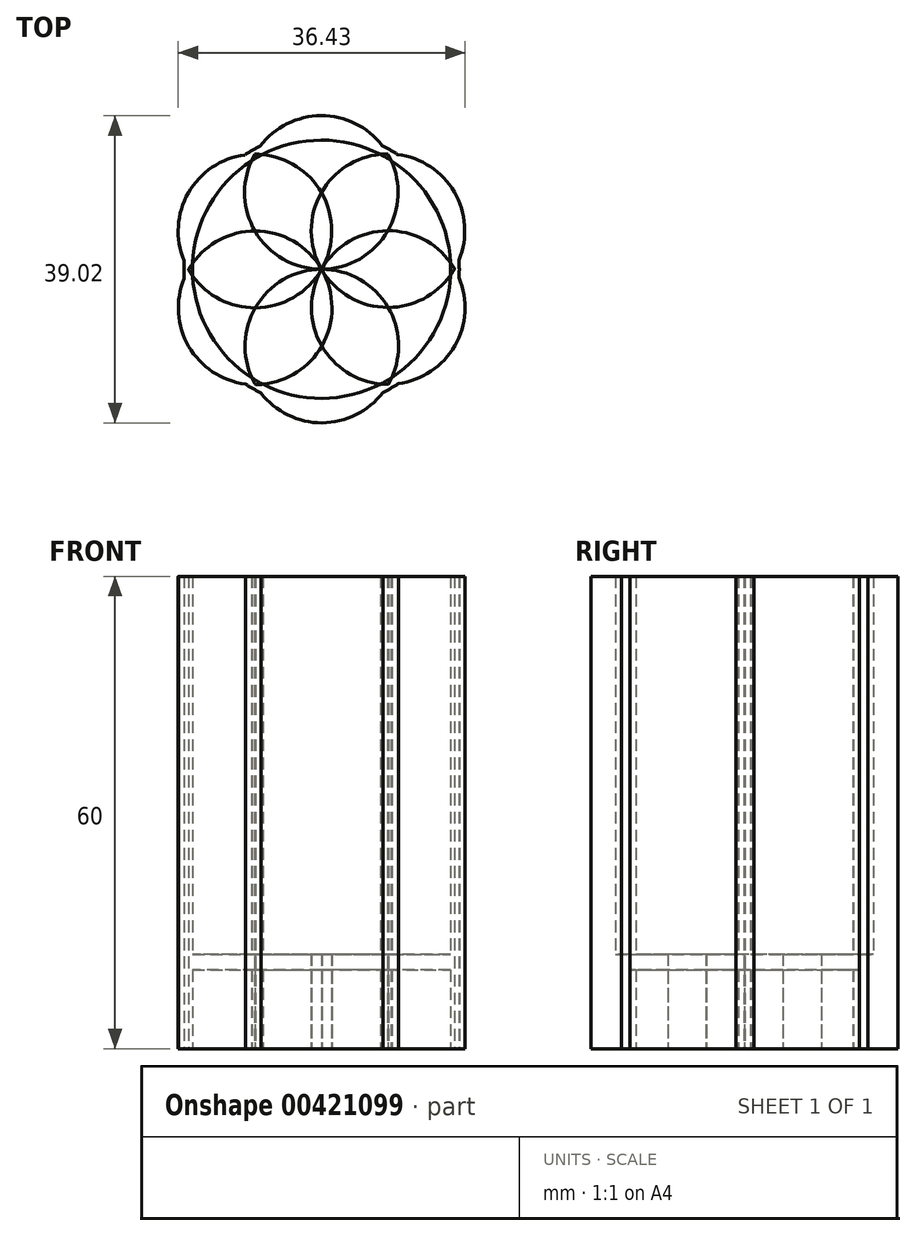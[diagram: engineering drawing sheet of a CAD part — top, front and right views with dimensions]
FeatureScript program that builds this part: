
annotation { "Feature Type Name" : "Feature", "Feature Type Description" : "" }
export const myFeature = defineFeature(function(context is Context, id is Id, definition is map)
    precondition{}
    {
        {
            var Q0;
            Q0=qCreatedBy(makeId("Top.planeOp"),FACE);
            var sketch = newSketch(context, id + "F0", { "sketchPlane" : qUnion([Q0])});
            skCircle(sketch, "E0", {"center": v(-40.7, 11.8) * mm, "radius": 9.75 * mm});
            skCircle(sketch, "E1", {"center": v(-32.26, 16.7) * mm, "radius": 9.75 * mm});
            skCircle(sketch, "E2", {"center": v(-32.23, 6.95) * mm, "radius": 9.75 * mm});
            skCircle(sketch, "E3", {"center": v(-40.66, 2.05) * mm, "radius": 9.75 * mm});
            skCircle(sketch, "E4", {"center": v(-49.13, 6.9) * mm, "radius": 9.75 * mm});
            skCircle(sketch, "E5", {"center": v(-49.15, 16.66) * mm, "radius": 9.75 * mm});
            skCircle(sketch, "E6", {"center": v(-40.72, 21.56) * mm, "radius": 9.75 * mm});
            skCircle(sketch, "E7", {"center": v(-40.7, 11.8) * mm, "radius": 13.06 * mm});
            skCircle(sketch, "E8", {"center": v(-40.7, 11.8) * mm, "radius": 14.2 * mm});
            skCircle(sketch, "E9", {"center": v(-40.7, 11.8) * mm, "radius": 15.33 * mm});
            skCircle(sketch, "E10", {"center": v(-40.7, 11.8) * mm, "radius": 16.4 * mm});
            skCircle(sketch, "E11", {"center": v(-40.7, 11.8) * mm, "radius": 17.5 * mm});
            skSolve(sketch);
        }
        {
            var Q0;
            Q0 = qSketchRegion(id + "F0", true);
            extrude(context, id + "F1", {"entities" : qUnion([Q0]), "depth" : 60 * mm});
        }
        {
            var Q0;
            {var subQ0=sQuery(id+"F0.wireOp",EDGE,"E9");var subQ1=sQuery(id+"F0.wireOp",EDGE,"E1");var subQ2=makeQuery(id+"F0.imprint","INTERSECT",VERTEX,{"disambiguationData":[OD(1.0)],"derivedFrom":[subQ1,subQ0]});Q0=makeQuery(id+"F0.imprint","IMPRINT",FACE,{"disambiguationData":[TD([[makeQuery(id+"F0.imprint","IMPRINT",EDGE,{"disambiguationData":[TD([[subQ2,-1.0]])],"derivedFrom":subQ1}),-1.0]])]});}
            var Q1;
            {var subQ0=sQuery(id+"F0.wireOp",EDGE,"E9");var subQ1=sQuery(id+"F0.wireOp",EDGE,"E2");var subQ2=makeQuery(id+"F0.imprint","INTERSECT",VERTEX,{"disambiguationData":[OD(1.0)],"derivedFrom":[subQ1,subQ0]});Q1=makeQuery(id+"F0.imprint","IMPRINT",FACE,{"disambiguationData":[TD([[makeQuery(id+"F0.imprint","IMPRINT",EDGE,{"disambiguationData":[TD([[subQ2,-1.0]])],"derivedFrom":subQ1}),-1.0]])]});}
            var Q2;
            {var subQ0=sQuery(id+"F0.wireOp",EDGE,"E10");var subQ1=sQuery(id+"F0.wireOp",EDGE,"E2");var subQ2=makeQuery(id+"F0.imprint","INTERSECT",VERTEX,{"disambiguationData":[OD(0.0)],"derivedFrom":[subQ1,subQ0]});Q2=makeQuery(id+"F0.imprint","IMPRINT",FACE,{"disambiguationData":[TD([[makeQuery(id+"F0.imprint","IMPRINT",EDGE,{"disambiguationData":[TD([[subQ2,-1.0]])],"derivedFrom":subQ1}),-1.0]])]});}
            var Q3;
            {var subQ0=sQuery(id+"F0.wireOp",EDGE,"E9");var subQ1=sQuery(id+"F0.wireOp",EDGE,"E2");var subQ2=makeQuery(id+"F0.imprint","INTERSECT",VERTEX,{"disambiguationData":[OD(0.0)],"derivedFrom":[subQ1,subQ0]});Q3=makeQuery(id+"F0.imprint","IMPRINT",FACE,{"disambiguationData":[TD([[makeQuery(id+"F0.imprint","IMPRINT",EDGE,{"disambiguationData":[TD([[subQ2,-1.0]])],"derivedFrom":subQ1}),-1.0]])]});}
            var Q4;
            {var subQ0=sQuery(id+"F0.wireOp",EDGE,"E8");var subQ1=sQuery(id+"F0.wireOp",EDGE,"E1");var subQ2=makeQuery(id+"F0.imprint","INTERSECT",VERTEX,{"disambiguationData":[OD(1.0)],"derivedFrom":[subQ1,subQ0]});Q4=makeQuery(id+"F0.imprint","IMPRINT",FACE,{"disambiguationData":[TD([[makeQuery(id+"F0.imprint","IMPRINT",EDGE,{"disambiguationData":[TD([[subQ2,-1.0]])],"derivedFrom":subQ1}),-1.0]])]});}
            var Q5;
            {var subQ0=sQuery(id+"F0.wireOp",EDGE,"E8");var subQ1=sQuery(id+"F0.wireOp",EDGE,"E2");var subQ2=makeQuery(id+"F0.imprint","INTERSECT",VERTEX,{"disambiguationData":[OD(1.0)],"derivedFrom":[subQ1,subQ0]});Q5=makeQuery(id+"F0.imprint","IMPRINT",FACE,{"disambiguationData":[TD([[makeQuery(id+"F0.imprint","IMPRINT",EDGE,{"disambiguationData":[TD([[subQ2,-1.0]])],"derivedFrom":subQ1}),-1.0]])]});}
            var Q6;
            {var subQ0=sQuery(id+"F0.wireOp",EDGE,"E7");var subQ1=sQuery(id+"F0.wireOp",EDGE,"E2");var subQ2=makeQuery(id+"F0.imprint","INTERSECT",VERTEX,{"disambiguationData":[OD(1.0)],"derivedFrom":[subQ1,subQ0]});Q6=makeQuery(id+"F0.imprint","IMPRINT",FACE,{"disambiguationData":[TD([[makeQuery(id+"F0.imprint","IMPRINT",EDGE,{"disambiguationData":[TD([[subQ2,-1.0]])],"derivedFrom":subQ1}),-1.0]])]});}
            var Q7;
            {var subQ0=sQuery(id+"F0.wireOp",EDGE,"E7");var subQ1=sQuery(id+"F0.wireOp",EDGE,"E1");var subQ2=makeQuery(id+"F0.imprint","INTERSECT",VERTEX,{"disambiguationData":[OD(1.0)],"derivedFrom":[subQ1,subQ0]});Q7=makeQuery(id+"F0.imprint","IMPRINT",FACE,{"disambiguationData":[TD([[makeQuery(id+"F0.imprint","IMPRINT",EDGE,{"disambiguationData":[TD([[subQ2,-1.0]])],"derivedFrom":subQ1}),-1.0]])]});}
            var Q8;
            {var subQ0=sQuery(id+"F0.wireOp",EDGE,"E8");var subQ1=sQuery(id+"F0.wireOp",EDGE,"E2");var subQ2=makeQuery(id+"F0.imprint","INTERSECT",VERTEX,{"disambiguationData":[OD(0.0)],"derivedFrom":[subQ1,subQ0]});Q8=makeQuery(id+"F0.imprint","IMPRINT",FACE,{"disambiguationData":[TD([[makeQuery(id+"F0.imprint","IMPRINT",EDGE,{"disambiguationData":[TD([[subQ2,-1.0]])],"derivedFrom":subQ1}),-1.0]])]});}
            var Q9;
            {var subQ0=sQuery(id+"F0.wireOp",EDGE,"E7");var subQ1=sQuery(id+"F0.wireOp",EDGE,"E2");var subQ2=makeQuery(id+"F0.imprint","INTERSECT",VERTEX,{"disambiguationData":[OD(1.0)],"derivedFrom":[subQ1,subQ0]});Q9=makeQuery(id+"F0.imprint","IMPRINT",FACE,{"disambiguationData":[TD([[makeQuery(id+"F0.imprint","IMPRINT",EDGE,{"disambiguationData":[TD([[subQ2,1.0]])],"derivedFrom":subQ0}),1.0]])]});}
            var Q10;
            {var subQ0=sQuery(id+"F0.wireOp",EDGE,"E7");var subQ1=sQuery(id+"F0.wireOp",EDGE,"E1");var subQ2=makeQuery(id+"F0.imprint","INTERSECT",VERTEX,{"disambiguationData":[OD(1.0)],"derivedFrom":[subQ1,subQ0]});Q10=makeQuery(id+"F0.imprint","IMPRINT",FACE,{"disambiguationData":[TD([[makeQuery(id+"F0.imprint","IMPRINT",EDGE,{"disambiguationData":[TD([[subQ2,1.0]])],"derivedFrom":subQ0}),1.0]])]});}
            var Q11;
            {var subQ0=sQuery(id+"F0.wireOp",EDGE,"E7");var subQ1=sQuery(id+"F0.wireOp",EDGE,"E2");var subQ2=makeQuery(id+"F0.imprint","INTERSECT",VERTEX,{"disambiguationData":[OD(0.0)],"derivedFrom":[subQ1,subQ0]});Q11=makeQuery(id+"F0.imprint","IMPRINT",FACE,{"disambiguationData":[TD([[makeQuery(id+"F0.imprint","IMPRINT",EDGE,{"disambiguationData":[TD([[subQ2,-1.0]])],"derivedFrom":subQ0}),1.0]])]});}
            var Q12;
            {var subQ0=sQuery(id+"F0.wireOp",EDGE,"E10");var subQ1=sQuery(id+"F0.wireOp",EDGE,"E1");var subQ2=makeQuery(id+"F0.imprint","INTERSECT",VERTEX,{"disambiguationData":[OD(0.0)],"derivedFrom":[subQ1,subQ0]});Q12=makeQuery(id+"F0.imprint","IMPRINT",FACE,{"disambiguationData":[TD([[makeQuery(id+"F0.imprint","IMPRINT",EDGE,{"disambiguationData":[TD([[subQ2,-1.0]])],"derivedFrom":subQ1}),-1.0]])]});}
            var Q13;
            {var subQ0=sQuery(id+"F0.wireOp",EDGE,"E9");var subQ1=sQuery(id+"F0.wireOp",EDGE,"E1");var subQ2=makeQuery(id+"F0.imprint","INTERSECT",VERTEX,{"disambiguationData":[OD(0.0)],"derivedFrom":[subQ1,subQ0]});Q13=makeQuery(id+"F0.imprint","IMPRINT",FACE,{"disambiguationData":[TD([[makeQuery(id+"F0.imprint","IMPRINT",EDGE,{"disambiguationData":[TD([[subQ2,-1.0]])],"derivedFrom":subQ1}),-1.0]])]});}
            var Q14;
            {var subQ0=sQuery(id+"F0.wireOp",EDGE,"E8");var subQ1=sQuery(id+"F0.wireOp",EDGE,"E1");var subQ2=makeQuery(id+"F0.imprint","INTERSECT",VERTEX,{"disambiguationData":[OD(0.0)],"derivedFrom":[subQ1,subQ0]});Q14=makeQuery(id+"F0.imprint","IMPRINT",FACE,{"disambiguationData":[TD([[makeQuery(id+"F0.imprint","IMPRINT",EDGE,{"disambiguationData":[TD([[subQ2,-1.0]])],"derivedFrom":subQ1}),-1.0]])]});}
            var Q15;
            {var subQ0=sQuery(id+"F0.wireOp",EDGE,"E7");var subQ1=sQuery(id+"F0.wireOp",EDGE,"E1");var subQ2=makeQuery(id+"F0.imprint","INTERSECT",VERTEX,{"disambiguationData":[OD(0.0)],"derivedFrom":[subQ1,subQ0]});Q15=makeQuery(id+"F0.imprint","IMPRINT",FACE,{"disambiguationData":[TD([[makeQuery(id+"F0.imprint","IMPRINT",EDGE,{"disambiguationData":[TD([[subQ2,-1.0]])],"derivedFrom":subQ0}),1.0]])]});}
            var Q16;
            {var subQ0=sQuery(id+"F0.wireOp",EDGE,"E9");var subQ1=sQuery(id+"F0.wireOp",EDGE,"E4");var subQ2=makeQuery(id+"F0.imprint","INTERSECT",VERTEX,{"disambiguationData":[OD(0.0)],"derivedFrom":[subQ1,subQ0]});Q16=makeQuery(id+"F0.imprint","IMPRINT",FACE,{"disambiguationData":[TD([[makeQuery(id+"F0.imprint","IMPRINT",EDGE,{"disambiguationData":[TD([[subQ2,-1.0]])],"derivedFrom":subQ1}),-1.0]])]});}
            var Q17;
            {var subQ0=sQuery(id+"F0.wireOp",EDGE,"E8");var subQ1=sQuery(id+"F0.wireOp",EDGE,"E4");var subQ2=makeQuery(id+"F0.imprint","INTERSECT",VERTEX,{"disambiguationData":[OD(0.0)],"derivedFrom":[subQ1,subQ0]});Q17=makeQuery(id+"F0.imprint","IMPRINT",FACE,{"disambiguationData":[TD([[makeQuery(id+"F0.imprint","IMPRINT",EDGE,{"disambiguationData":[TD([[subQ2,-1.0]])],"derivedFrom":subQ1}),-1.0]])]});}
            var Q18;
            {var subQ0=sQuery(id+"F0.wireOp",EDGE,"E7");var subQ1=sQuery(id+"F0.wireOp",EDGE,"E4");var subQ2=makeQuery(id+"F0.imprint","INTERSECT",VERTEX,{"disambiguationData":[OD(0.0)],"derivedFrom":[subQ1,subQ0]});Q18=makeQuery(id+"F0.imprint","IMPRINT",FACE,{"disambiguationData":[TD([[makeQuery(id+"F0.imprint","IMPRINT",EDGE,{"disambiguationData":[TD([[subQ2,-1.0]])],"derivedFrom":subQ1}),-1.0]])]});}
            var Q19;
            {var subQ0=sQuery(id+"F0.wireOp",EDGE,"E7");var subQ1=sQuery(id+"F0.wireOp",EDGE,"E4");var subQ2=makeQuery(id+"F0.imprint","INTERSECT",VERTEX,{"disambiguationData":[OD(0.0)],"derivedFrom":[subQ1,subQ0]});Q19=makeQuery(id+"F0.imprint","IMPRINT",FACE,{"disambiguationData":[TD([[makeQuery(id+"F0.imprint","IMPRINT",EDGE,{"disambiguationData":[TD([[subQ2,1.0]])],"derivedFrom":subQ0}),1.0]])]});}
            var Q20;
            {var subQ0=sQuery(id+"F0.wireOp",EDGE,"E9");var subQ1=sQuery(id+"F0.wireOp",EDGE,"E3");var subQ2=makeQuery(id+"F0.imprint","INTERSECT",VERTEX,{"disambiguationData":[OD(0.0)],"derivedFrom":[subQ1,subQ0]});Q20=makeQuery(id+"F0.imprint","IMPRINT",FACE,{"disambiguationData":[TD([[makeQuery(id+"F0.imprint","IMPRINT",EDGE,{"disambiguationData":[TD([[subQ2,-1.0]])],"derivedFrom":subQ1}),-1.0]])]});}
            var Q21;
            {var subQ0=sQuery(id+"F0.wireOp",EDGE,"E8");var subQ1=sQuery(id+"F0.wireOp",EDGE,"E3");var subQ2=makeQuery(id+"F0.imprint","INTERSECT",VERTEX,{"disambiguationData":[OD(0.0)],"derivedFrom":[subQ1,subQ0]});Q21=makeQuery(id+"F0.imprint","IMPRINT",FACE,{"disambiguationData":[TD([[makeQuery(id+"F0.imprint","IMPRINT",EDGE,{"disambiguationData":[TD([[subQ2,-1.0]])],"derivedFrom":subQ1}),-1.0]])]});}
            var Q22;
            {var subQ0=sQuery(id+"F0.wireOp",EDGE,"E7");var subQ1=sQuery(id+"F0.wireOp",EDGE,"E3");var subQ2=makeQuery(id+"F0.imprint","INTERSECT",VERTEX,{"disambiguationData":[OD(1.0)],"derivedFrom":[subQ1,subQ0]});Q22=makeQuery(id+"F0.imprint","IMPRINT",FACE,{"disambiguationData":[TD([[makeQuery(id+"F0.imprint","IMPRINT",EDGE,{"disambiguationData":[TD([[subQ2,-1.0]])],"derivedFrom":subQ1}),-1.0]])]});}
            var Q23;
            {var subQ0=sQuery(id+"F0.wireOp",EDGE,"E7");var subQ1=sQuery(id+"F0.wireOp",EDGE,"E3");var subQ2=makeQuery(id+"F0.imprint","INTERSECT",VERTEX,{"disambiguationData":[OD(1.0)],"derivedFrom":[subQ1,subQ0]});Q23=makeQuery(id+"F0.imprint","IMPRINT",FACE,{"disambiguationData":[TD([[makeQuery(id+"F0.imprint","IMPRINT",EDGE,{"disambiguationData":[TD([[subQ2,1.0]])],"derivedFrom":subQ0}),1.0]])]});}
            var Q24;
            {var subQ0=sQuery(id+"F0.wireOp",EDGE,"E5");var subQ1=sQuery(id+"F0.wireOp",EDGE,"E1");var subQ2=makeQuery(id+"F0.imprint","INTERSECT",VERTEX,{"derivedFrom":[sQuery(id+"F0.wireOp",EDGE,"E0"),subQ1,subQ0]});Q24=makeQuery(id+"F0.imprint","IMPRINT",FACE,{"disambiguationData":[TD([[makeQuery(id+"F0.imprint","IMPRINT",EDGE,{"disambiguationData":[TD([[subQ2,-1.0]])],"derivedFrom":subQ1}),1.0]])]});}
            var Q25;
            {var subQ0=sQuery(id+"F0.wireOp",EDGE,"E6");var subQ1=sQuery(id+"F0.wireOp",EDGE,"E2");var subQ2=makeQuery(id+"F0.imprint","INTERSECT",VERTEX,{"derivedFrom":[sQuery(id+"F0.wireOp",EDGE,"E0"),subQ1,subQ0]});Q25=makeQuery(id+"F0.imprint","IMPRINT",FACE,{"disambiguationData":[TD([[makeQuery(id+"F0.imprint","IMPRINT",EDGE,{"disambiguationData":[TD([[subQ2,-1.0]])],"derivedFrom":subQ1}),1.0]])]});}
            var Q26;
            {var subQ0=sQuery(id+"F0.wireOp",EDGE,"E3");var subQ1=sQuery(id+"F0.wireOp",EDGE,"E1");var subQ2=makeQuery(id+"F0.imprint","INTERSECT",VERTEX,{"derivedFrom":[sQuery(id+"F0.wireOp",EDGE,"E0"),subQ1,subQ0]});Q26=makeQuery(id+"F0.imprint","IMPRINT",FACE,{"disambiguationData":[TD([[makeQuery(id+"F0.imprint","IMPRINT",EDGE,{"disambiguationData":[TD([[subQ2,1.0]])],"derivedFrom":subQ1}),1.0]])]});}
            var Q27;
            {var subQ0=sQuery(id+"F0.wireOp",EDGE,"E4");var subQ1=sQuery(id+"F0.wireOp",EDGE,"E2");var subQ2=makeQuery(id+"F0.imprint","INTERSECT",VERTEX,{"derivedFrom":[sQuery(id+"F0.wireOp",EDGE,"E0"),subQ1,subQ0]});Q27=makeQuery(id+"F0.imprint","IMPRINT",FACE,{"disambiguationData":[TD([[makeQuery(id+"F0.imprint","IMPRINT",EDGE,{"disambiguationData":[TD([[subQ2,1.0]])],"derivedFrom":subQ1}),1.0]])]});}
            var Q28;
            {var subQ0=sQuery(id+"F0.wireOp",EDGE,"E5");var subQ1=sQuery(id+"F0.wireOp",EDGE,"E3");var subQ2=makeQuery(id+"F0.imprint","INTERSECT",VERTEX,{"derivedFrom":[sQuery(id+"F0.wireOp",EDGE,"E0"),subQ1,subQ0]});Q28=makeQuery(id+"F0.imprint","IMPRINT",FACE,{"disambiguationData":[TD([[makeQuery(id+"F0.imprint","IMPRINT",EDGE,{"disambiguationData":[TD([[subQ2,1.0]])],"derivedFrom":subQ1}),1.0]])]});}
            var Q29;
            {var subQ0=sQuery(id+"F0.wireOp",EDGE,"E6");var subQ1=sQuery(id+"F0.wireOp",EDGE,"E4");var subQ2=makeQuery(id+"F0.imprint","INTERSECT",VERTEX,{"derivedFrom":[sQuery(id+"F0.wireOp",EDGE,"E0"),subQ1,subQ0]});Q29=makeQuery(id+"F0.imprint","IMPRINT",FACE,{"disambiguationData":[TD([[makeQuery(id+"F0.imprint","IMPRINT",EDGE,{"disambiguationData":[TD([[subQ2,1.0]])],"derivedFrom":subQ1}),1.0]])]});}
            extrude(context, id + "F2", {"entities" : qUnion([Q0, Q1, Q2, Q3, Q4, Q5, Q6, Q7, Q8, Q9, Q10, Q11, Q12, Q13, Q14, Q15, Q16, Q17, Q18, Q19, Q20, Q21, Q22, Q23, Q24, Q25, Q26, Q27, Q28, Q29]), "operationType" : NewBodyOperationType.ADD, "depth" : 12 * mm});
        }
        {
            var Q0;
            {var subQ0=sQuery(id+"F0.wireOp",EDGE,"E1");var subQ5=sQuery(id+"F0.wireOp",EDGE,"E7");var subQ6=makeQuery(id+"F0.imprint","INTERSECT",VERTEX,{"disambiguationData":[OD(0.0)],"derivedFrom":[subQ0,subQ5]});Q0=makeQuery(id+"F0.imprint","IMPRINT",FACE,{"disambiguationData":[TD([[makeQuery(id+"F0.imprint","IMPRINT",EDGE,{"disambiguationData":[TD([[subQ6,1.0]])],"derivedFrom":subQ5}),1.0]])]});}
            var Q1;
            {var subQ0=sQuery(id+"F0.wireOp",EDGE,"E8");var subQ1=sQuery(id+"F0.wireOp",EDGE,"E1");var subQ2=makeQuery(id+"F0.imprint","INTERSECT",VERTEX,{"disambiguationData":[OD(0.0)],"derivedFrom":[subQ1,subQ0]});Q1=makeQuery(id+"F0.imprint","IMPRINT",FACE,{"disambiguationData":[TD([[makeQuery(id+"F0.imprint","IMPRINT",EDGE,{"disambiguationData":[TD([[subQ2,-1.0]])],"derivedFrom":subQ1}),1.0]])]});}
            var Q2;
            {var subQ0=sQuery(id+"F0.wireOp",EDGE,"E9");var subQ1=sQuery(id+"F0.wireOp",EDGE,"E1");var subQ2=makeQuery(id+"F0.imprint","INTERSECT",VERTEX,{"disambiguationData":[OD(0.0)],"derivedFrom":[subQ1,subQ0]});Q2=makeQuery(id+"F0.imprint","IMPRINT",FACE,{"disambiguationData":[TD([[makeQuery(id+"F0.imprint","IMPRINT",EDGE,{"disambiguationData":[TD([[subQ2,-1.0]])],"derivedFrom":subQ1}),1.0]])]});}
            var Q3;
            {var subQ0=sQuery(id+"F0.wireOp",EDGE,"E10");var subQ1=sQuery(id+"F0.wireOp",EDGE,"E1");var subQ2=makeQuery(id+"F0.imprint","INTERSECT",VERTEX,{"disambiguationData":[OD(0.0)],"derivedFrom":[subQ1,subQ0]});Q3=makeQuery(id+"F0.imprint","IMPRINT",FACE,{"disambiguationData":[TD([[makeQuery(id+"F0.imprint","IMPRINT",EDGE,{"disambiguationData":[TD([[subQ2,-1.0]])],"derivedFrom":subQ1}),1.0]])]});}
            var Q4;
            {var subQ0=sQuery(id+"F0.wireOp",EDGE,"E5");var subQ1=sQuery(id+"F0.wireOp",EDGE,"E1");var subQ2=sQuery(id+"F0.wireOp",EDGE,"E0");var subQ3=makeQuery(id+"F0.imprint","INTERSECT",VERTEX,{"derivedFrom":[subQ2,subQ1,subQ0]});Q4=makeQuery(id+"F0.imprint","IMPRINT",FACE,{"disambiguationData":[TD([[makeQuery(id+"F0.imprint","IMPRINT",EDGE,{"disambiguationData":[TD([[subQ3,1.0]])],"derivedFrom":subQ2}),1.0]])]});}
            var Q5;
            {var subQ0=sQuery(id+"F0.wireOp",EDGE,"E6");var subQ1=sQuery(id+"F0.wireOp",EDGE,"E2");var subQ2=sQuery(id+"F0.wireOp",EDGE,"E0");var subQ3=makeQuery(id+"F0.imprint","INTERSECT",VERTEX,{"derivedFrom":[subQ2,subQ1,subQ0]});Q5=makeQuery(id+"F0.imprint","IMPRINT",FACE,{"disambiguationData":[TD([[makeQuery(id+"F0.imprint","IMPRINT",EDGE,{"disambiguationData":[TD([[subQ3,1.0]])],"derivedFrom":subQ2}),1.0]])]});}
            var Q6;
            {var subQ3=sQuery(id+"F0.wireOp",EDGE,"E1");var subQ5=sQuery(id+"F0.wireOp",EDGE,"E7");var subQ6=makeQuery(id+"F0.imprint","INTERSECT",VERTEX,{"disambiguationData":[OD(1.0)],"derivedFrom":[subQ3,subQ5]});Q6=makeQuery(id+"F0.imprint","IMPRINT",FACE,{"disambiguationData":[TD([[makeQuery(id+"F0.imprint","IMPRINT",EDGE,{"disambiguationData":[TD([[subQ6,-1.0]])],"derivedFrom":subQ5}),1.0]])]});}
            var Q7;
            {var subQ0=sQuery(id+"F0.wireOp",EDGE,"E7");var subQ1=sQuery(id+"F0.wireOp",EDGE,"E1");var subQ2=makeQuery(id+"F0.imprint","INTERSECT",VERTEX,{"disambiguationData":[OD(1.0)],"derivedFrom":[subQ1,subQ0]});Q7=makeQuery(id+"F0.imprint","IMPRINT",FACE,{"disambiguationData":[TD([[makeQuery(id+"F0.imprint","IMPRINT",EDGE,{"disambiguationData":[TD([[subQ2,-1.0]])],"derivedFrom":subQ1}),1.0]])]});}
            var Q8;
            {var subQ0=sQuery(id+"F0.wireOp",EDGE,"E8");var subQ1=sQuery(id+"F0.wireOp",EDGE,"E1");var subQ2=makeQuery(id+"F0.imprint","INTERSECT",VERTEX,{"disambiguationData":[OD(1.0)],"derivedFrom":[subQ1,subQ0]});Q8=makeQuery(id+"F0.imprint","IMPRINT",FACE,{"disambiguationData":[TD([[makeQuery(id+"F0.imprint","IMPRINT",EDGE,{"disambiguationData":[TD([[subQ2,-1.0]])],"derivedFrom":subQ1}),1.0]])]});}
            var Q9;
            {var subQ0=sQuery(id+"F0.wireOp",EDGE,"E9");var subQ1=sQuery(id+"F0.wireOp",EDGE,"E1");var subQ2=makeQuery(id+"F0.imprint","INTERSECT",VERTEX,{"disambiguationData":[OD(1.0)],"derivedFrom":[subQ1,subQ0]});Q9=makeQuery(id+"F0.imprint","IMPRINT",FACE,{"disambiguationData":[TD([[makeQuery(id+"F0.imprint","IMPRINT",EDGE,{"disambiguationData":[TD([[subQ2,-1.0]])],"derivedFrom":subQ1}),1.0]])]});}
            var Q10;
            {var subQ0=sQuery(id+"F0.wireOp",EDGE,"E4");var subQ1=sQuery(id+"F0.wireOp",EDGE,"E2");var subQ2=sQuery(id+"F0.wireOp",EDGE,"E0");var subQ3=makeQuery(id+"F0.imprint","INTERSECT",VERTEX,{"derivedFrom":[subQ2,subQ1,subQ0]});Q10=makeQuery(id+"F0.imprint","IMPRINT",FACE,{"disambiguationData":[TD([[makeQuery(id+"F0.imprint","IMPRINT",EDGE,{"disambiguationData":[TD([[subQ3,-1.0]])],"derivedFrom":subQ2}),1.0]])]});}
            var Q11;
            {var subQ0=sQuery(id+"F0.wireOp",EDGE,"E2");var subQ5=sQuery(id+"F0.wireOp",EDGE,"E7");var subQ6=makeQuery(id+"F0.imprint","INTERSECT",VERTEX,{"disambiguationData":[OD(1.0)],"derivedFrom":[subQ0,subQ5]});Q11=makeQuery(id+"F0.imprint","IMPRINT",FACE,{"disambiguationData":[TD([[makeQuery(id+"F0.imprint","IMPRINT",EDGE,{"disambiguationData":[TD([[subQ6,-1.0]])],"derivedFrom":subQ5}),1.0]])]});}
            var Q12;
            {var subQ0=sQuery(id+"F0.wireOp",EDGE,"E7");var subQ1=sQuery(id+"F0.wireOp",EDGE,"E2");var subQ2=makeQuery(id+"F0.imprint","INTERSECT",VERTEX,{"disambiguationData":[OD(1.0)],"derivedFrom":[subQ1,subQ0]});Q12=makeQuery(id+"F0.imprint","IMPRINT",FACE,{"disambiguationData":[TD([[makeQuery(id+"F0.imprint","IMPRINT",EDGE,{"disambiguationData":[TD([[subQ2,-1.0]])],"derivedFrom":subQ1}),1.0]])]});}
            var Q13;
            {var subQ0=sQuery(id+"F0.wireOp",EDGE,"E8");var subQ1=sQuery(id+"F0.wireOp",EDGE,"E2");var subQ2=makeQuery(id+"F0.imprint","INTERSECT",VERTEX,{"disambiguationData":[OD(1.0)],"derivedFrom":[subQ1,subQ0]});Q13=makeQuery(id+"F0.imprint","IMPRINT",FACE,{"disambiguationData":[TD([[makeQuery(id+"F0.imprint","IMPRINT",EDGE,{"disambiguationData":[TD([[subQ2,-1.0]])],"derivedFrom":subQ1}),1.0]])]});}
            var Q14;
            {var subQ0=sQuery(id+"F0.wireOp",EDGE,"E9");var subQ1=sQuery(id+"F0.wireOp",EDGE,"E2");var subQ2=makeQuery(id+"F0.imprint","INTERSECT",VERTEX,{"disambiguationData":[OD(1.0)],"derivedFrom":[subQ1,subQ0]});Q14=makeQuery(id+"F0.imprint","IMPRINT",FACE,{"disambiguationData":[TD([[makeQuery(id+"F0.imprint","IMPRINT",EDGE,{"disambiguationData":[TD([[subQ2,-1.0]])],"derivedFrom":subQ1}),1.0]])]});}
            var Q15;
            {var subQ0=sQuery(id+"F0.wireOp",EDGE,"E3");var subQ5=sQuery(id+"F0.wireOp",EDGE,"E7");var subQ6=makeQuery(id+"F0.imprint","INTERSECT",VERTEX,{"disambiguationData":[OD(1.0)],"derivedFrom":[subQ0,subQ5]});Q15=makeQuery(id+"F0.imprint","IMPRINT",FACE,{"disambiguationData":[TD([[makeQuery(id+"F0.imprint","IMPRINT",EDGE,{"disambiguationData":[TD([[subQ6,-1.0]])],"derivedFrom":subQ5}),1.0]])]});}
            var Q16;
            {var subQ0=sQuery(id+"F0.wireOp",EDGE,"E7");var subQ1=sQuery(id+"F0.wireOp",EDGE,"E3");var subQ2=makeQuery(id+"F0.imprint","INTERSECT",VERTEX,{"disambiguationData":[OD(1.0)],"derivedFrom":[subQ1,subQ0]});Q16=makeQuery(id+"F0.imprint","IMPRINT",FACE,{"disambiguationData":[TD([[makeQuery(id+"F0.imprint","IMPRINT",EDGE,{"disambiguationData":[TD([[subQ2,-1.0]])],"derivedFrom":subQ1}),1.0]])]});}
            var Q17;
            {var subQ0=sQuery(id+"F0.wireOp",EDGE,"E8");var subQ1=sQuery(id+"F0.wireOp",EDGE,"E3");var subQ2=makeQuery(id+"F0.imprint","INTERSECT",VERTEX,{"disambiguationData":[OD(0.0)],"derivedFrom":[subQ1,subQ0]});Q17=makeQuery(id+"F0.imprint","IMPRINT",FACE,{"disambiguationData":[TD([[makeQuery(id+"F0.imprint","IMPRINT",EDGE,{"disambiguationData":[TD([[subQ2,-1.0]])],"derivedFrom":subQ1}),1.0]])]});}
            var Q18;
            {var subQ0=sQuery(id+"F0.wireOp",EDGE,"E9");var subQ1=sQuery(id+"F0.wireOp",EDGE,"E3");var subQ2=makeQuery(id+"F0.imprint","INTERSECT",VERTEX,{"disambiguationData":[OD(0.0)],"derivedFrom":[subQ1,subQ0]});Q18=makeQuery(id+"F0.imprint","IMPRINT",FACE,{"disambiguationData":[TD([[makeQuery(id+"F0.imprint","IMPRINT",EDGE,{"disambiguationData":[TD([[subQ2,-1.0]])],"derivedFrom":subQ1}),1.0]])]});}
            var Q19;
            {var subQ0=sQuery(id+"F0.wireOp",EDGE,"E5");var subQ1=sQuery(id+"F0.wireOp",EDGE,"E3");var subQ2=sQuery(id+"F0.wireOp",EDGE,"E0");var subQ3=makeQuery(id+"F0.imprint","INTERSECT",VERTEX,{"derivedFrom":[subQ2,subQ1,subQ0]});Q19=makeQuery(id+"F0.imprint","IMPRINT",FACE,{"disambiguationData":[TD([[makeQuery(id+"F0.imprint","IMPRINT",EDGE,{"disambiguationData":[TD([[subQ3,-1.0]])],"derivedFrom":subQ2}),1.0]])]});}
            var Q20;
            {var subQ0=sQuery(id+"F0.wireOp",EDGE,"E9");var subQ1=sQuery(id+"F0.wireOp",EDGE,"E4");var subQ2=makeQuery(id+"F0.imprint","INTERSECT",VERTEX,{"disambiguationData":[OD(0.0)],"derivedFrom":[subQ1,subQ0]});Q20=makeQuery(id+"F0.imprint","IMPRINT",FACE,{"disambiguationData":[TD([[makeQuery(id+"F0.imprint","IMPRINT",EDGE,{"disambiguationData":[TD([[subQ2,-1.0]])],"derivedFrom":subQ1}),1.0]])]});}
            var Q21;
            {var subQ0=sQuery(id+"F0.wireOp",EDGE,"E8");var subQ1=sQuery(id+"F0.wireOp",EDGE,"E4");var subQ2=makeQuery(id+"F0.imprint","INTERSECT",VERTEX,{"disambiguationData":[OD(0.0)],"derivedFrom":[subQ1,subQ0]});Q21=makeQuery(id+"F0.imprint","IMPRINT",FACE,{"disambiguationData":[TD([[makeQuery(id+"F0.imprint","IMPRINT",EDGE,{"disambiguationData":[TD([[subQ2,-1.0]])],"derivedFrom":subQ1}),1.0]])]});}
            var Q22;
            {var subQ0=sQuery(id+"F0.wireOp",EDGE,"E7");var subQ1=sQuery(id+"F0.wireOp",EDGE,"E4");var subQ2=makeQuery(id+"F0.imprint","INTERSECT",VERTEX,{"disambiguationData":[OD(0.0)],"derivedFrom":[subQ1,subQ0]});Q22=makeQuery(id+"F0.imprint","IMPRINT",FACE,{"disambiguationData":[TD([[makeQuery(id+"F0.imprint","IMPRINT",EDGE,{"disambiguationData":[TD([[subQ2,-1.0]])],"derivedFrom":subQ1}),1.0]])]});}
            var Q23;
            {var subQ0=sQuery(id+"F0.wireOp",EDGE,"E4");var subQ5=sQuery(id+"F0.wireOp",EDGE,"E7");var subQ6=makeQuery(id+"F0.imprint","INTERSECT",VERTEX,{"disambiguationData":[OD(0.0)],"derivedFrom":[subQ0,subQ5]});Q23=makeQuery(id+"F0.imprint","IMPRINT",FACE,{"disambiguationData":[TD([[makeQuery(id+"F0.imprint","IMPRINT",EDGE,{"disambiguationData":[TD([[subQ6,-1.0]])],"derivedFrom":subQ5}),1.0]])]});}
            var Q24;
            {var subQ0=sQuery(id+"F0.wireOp",EDGE,"E6");var subQ1=sQuery(id+"F0.wireOp",EDGE,"E4");var subQ2=sQuery(id+"F0.wireOp",EDGE,"E0");var subQ3=makeQuery(id+"F0.imprint","INTERSECT",VERTEX,{"derivedFrom":[subQ2,subQ1,subQ0]});Q24=makeQuery(id+"F0.imprint","IMPRINT",FACE,{"disambiguationData":[TD([[makeQuery(id+"F0.imprint","IMPRINT",EDGE,{"disambiguationData":[TD([[subQ3,-1.0]])],"derivedFrom":subQ2}),1.0]])]});}
            var Q25;
            {var subQ0=sQuery(id+"F0.wireOp",EDGE,"E5");var subQ1=sQuery(id+"F0.wireOp",EDGE,"E1");var subQ2=sQuery(id+"F0.wireOp",EDGE,"E0");var subQ3=makeQuery(id+"F0.imprint","INTERSECT",VERTEX,{"derivedFrom":[subQ2,subQ1,subQ0]});Q25=makeQuery(id+"F0.imprint","IMPRINT",FACE,{"disambiguationData":[TD([[makeQuery(id+"F0.imprint","IMPRINT",EDGE,{"disambiguationData":[TD([[subQ3,-1.0]])],"derivedFrom":subQ2}),1.0]])]});}
            var Q26;
            {var subQ0=sQuery(id+"F0.wireOp",EDGE,"E5");var subQ5=sQuery(id+"F0.wireOp",EDGE,"E7");var subQ6=makeQuery(id+"F0.imprint","INTERSECT",VERTEX,{"disambiguationData":[OD(0.0)],"derivedFrom":[subQ0,subQ5]});Q26=makeQuery(id+"F0.imprint","IMPRINT",FACE,{"disambiguationData":[TD([[makeQuery(id+"F0.imprint","IMPRINT",EDGE,{"disambiguationData":[TD([[subQ6,-1.0]])],"derivedFrom":subQ5}),1.0]])]});}
            var Q27;
            {var subQ0=sQuery(id+"F0.wireOp",EDGE,"E9");var subQ1=sQuery(id+"F0.wireOp",EDGE,"E5");var subQ2=makeQuery(id+"F0.imprint","INTERSECT",VERTEX,{"disambiguationData":[OD(0.0)],"derivedFrom":[subQ1,subQ0]});Q27=makeQuery(id+"F0.imprint","IMPRINT",FACE,{"disambiguationData":[TD([[makeQuery(id+"F0.imprint","IMPRINT",EDGE,{"disambiguationData":[TD([[subQ2,-1.0]])],"derivedFrom":subQ1}),1.0]])]});}
            var Q28;
            {var subQ0=sQuery(id+"F0.wireOp",EDGE,"E8");var subQ1=sQuery(id+"F0.wireOp",EDGE,"E5");var subQ2=makeQuery(id+"F0.imprint","INTERSECT",VERTEX,{"disambiguationData":[OD(0.0)],"derivedFrom":[subQ1,subQ0]});Q28=makeQuery(id+"F0.imprint","IMPRINT",FACE,{"disambiguationData":[TD([[makeQuery(id+"F0.imprint","IMPRINT",EDGE,{"disambiguationData":[TD([[subQ2,-1.0]])],"derivedFrom":subQ1}),1.0]])]});}
            var Q29;
            {var subQ0=sQuery(id+"F0.wireOp",EDGE,"E7");var subQ1=sQuery(id+"F0.wireOp",EDGE,"E5");var subQ2=makeQuery(id+"F0.imprint","INTERSECT",VERTEX,{"disambiguationData":[OD(0.0)],"derivedFrom":[subQ1,subQ0]});Q29=makeQuery(id+"F0.imprint","IMPRINT",FACE,{"disambiguationData":[TD([[makeQuery(id+"F0.imprint","IMPRINT",EDGE,{"disambiguationData":[TD([[subQ2,-1.0]])],"derivedFrom":subQ1}),1.0]])]});}
            extrude(context, id + "F3", {"entities" : qUnion([Q0, Q1, Q2, Q3, Q4, Q5, Q6, Q7, Q8, Q9, Q10, Q11, Q12, Q13, Q14, Q15, Q16, Q17, Q18, Q19, Q20, Q21, Q22, Q23, Q24, Q25, Q26, Q27, Q28, Q29]), "depth" : 10 * mm});
        }
    });
